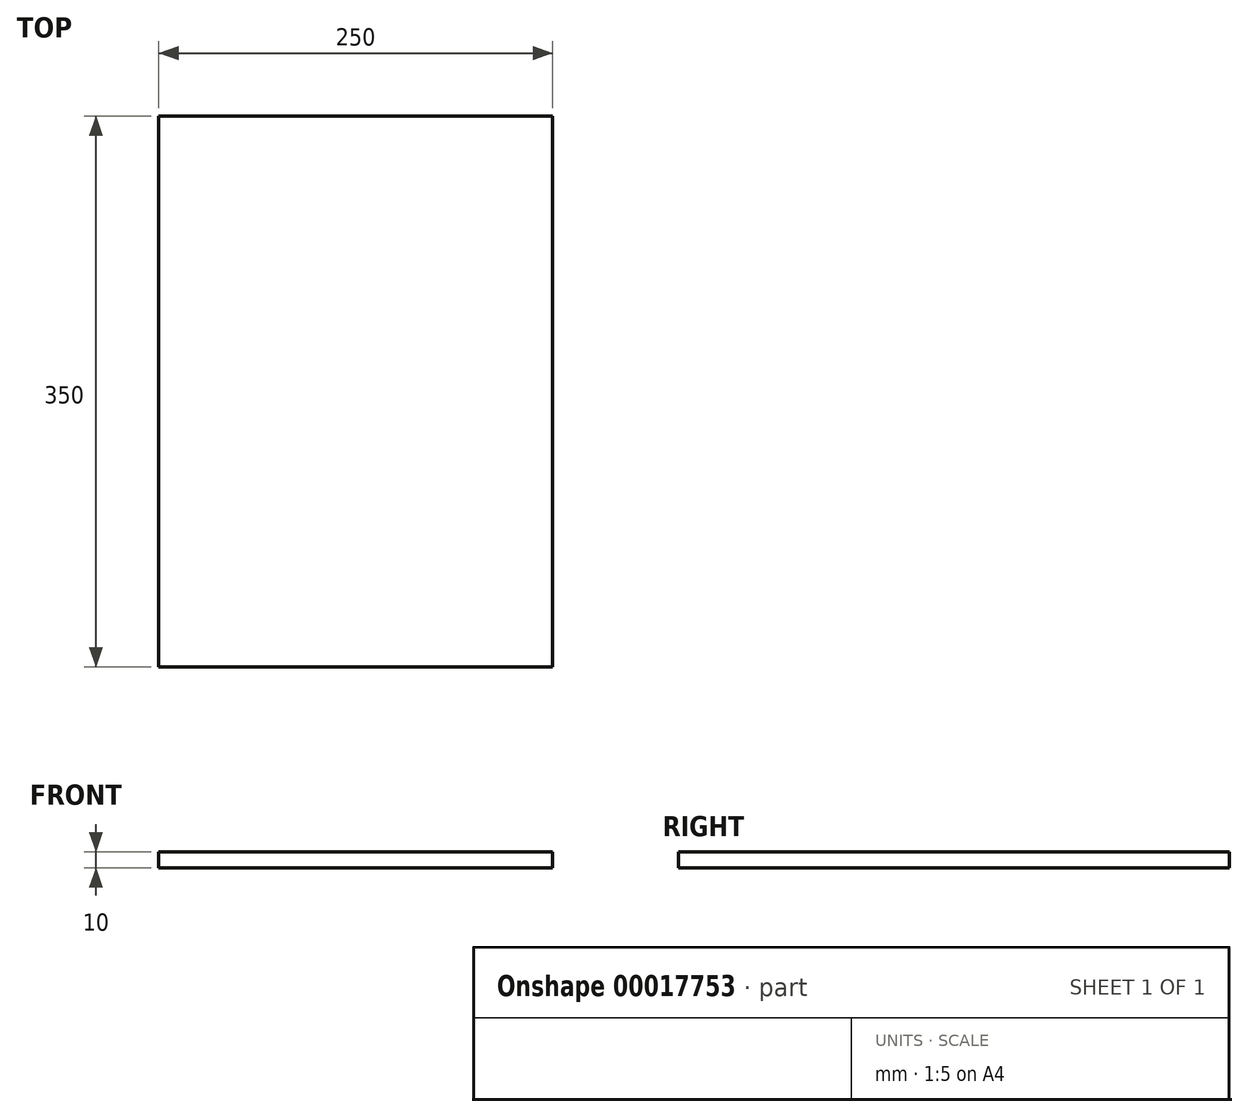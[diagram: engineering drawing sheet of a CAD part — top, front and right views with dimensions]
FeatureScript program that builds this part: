
annotation { "Feature Type Name" : "Feature", "Feature Type Description" : "" }
export const myFeature = defineFeature(function(context is Context, id is Id, definition is map)
    precondition{}
    {
        {
            var Q0;
            Q0=qCreatedBy(makeId("Top.planeOp"),FACE);
            var sketch = newSketch(context, id + "F0", { "sketchPlane" : qUnion([Q0])});
            skLineSegment(sketch, "E0.bottom", {"start": v(-44.88, 208.19) * mm, "end": v(205.12, 208.19) * mm});
            skLineSegment(sketch, "E0.top", {"start": v(-44.88, -141.81) * mm, "end": v(205.12, -141.81) * mm});
            skLineSegment(sketch, "E0.left", {"start": v(-44.88, 208.19) * mm, "end": v(-44.88, -141.81) * mm});
            skLineSegment(sketch, "E0.right", {"start": v(205.12, 208.19) * mm, "end": v(205.12, -141.81) * mm});
            skSolve(sketch);
        }
        {
            var Q0;
            Q0=qSketchRegion(id+"F0",true);
            extrude(context, id + "F1", {"entities" : qUnion([Q0]), "depth" : 10 * mm});
        }
    });
